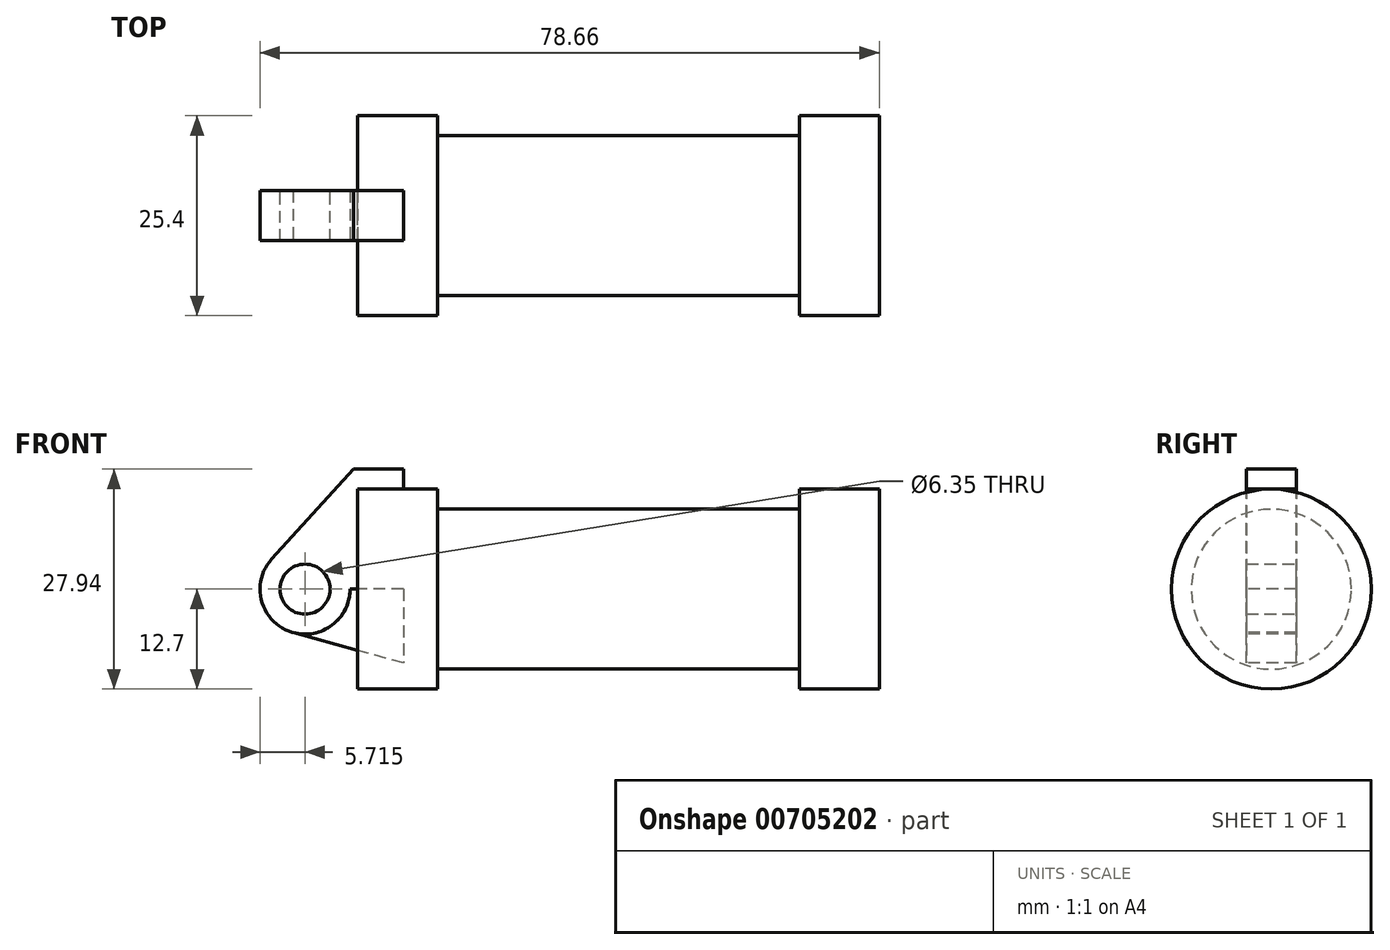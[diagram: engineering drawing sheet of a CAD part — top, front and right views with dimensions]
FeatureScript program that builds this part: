
annotation { "Feature Type Name" : "Feature", "Feature Type Description" : "" }
export const myFeature = defineFeature(function(context is Context, id is Id, definition is map)
    precondition{}
    {
        {
            var Q0;
            Q0=qCreatedBy(makeId("Front.planeOp"),FACE);
            var sketch = newSketch(context, id + "F0", { "sketchPlane" : qUnion([Q0])});
            skLineSegment(sketch, "E0", {"start": v(0, 0) * mm, "end": v(0, 12.7) * mm});
            skLineSegment(sketch, "E1", {"start": v(0, 12.7) * mm, "end": v(10.16, 12.7) * mm});
            skLineSegment(sketch, "E2", {"start": v(10.16, 12.7) * mm, "end": v(10.16, 10.16) * mm});
            skLineSegment(sketch, "E3", {"start": v(10.16, 10.16) * mm, "end": v(56.13, 10.16) * mm});
            skLineSegment(sketch, "E4", {"start": v(56.13, 10.16) * mm, "end": v(56.13, 12.7) * mm});
            skLineSegment(sketch, "E5", {"start": v(56.13, 12.7) * mm, "end": v(66.3, 12.7) * mm});
            skLineSegment(sketch, "E6", {"start": v(66.3, 12.7) * mm, "end": v(66.3, 0) * mm});
            skLineSegment(sketch, "E7", {"start": v(66.3, 0) * mm, "end": v(0, 0) * mm});
            skLineSegment(sketch, "E8", {"start": v(5.84, 15.24) * mm, "end": v(-0.5, 15.24) * mm});
            skLineSegment(sketch, "E9", {"start": v(-0.5, 15.24) * mm, "end": v(-10.88, 3.85) * mm});
            skLineSegment(sketch, "E10", {"start": v(0, 0) * mm, "end": v(-6.65, 0) * mm});
            skCircle(sketch, "E11", {"center": v(-6.65, 0) * mm, "radius": 5.72 * mm});
            skCircle(sketch, "E12", {"center": v(-6.65, 0) * mm, "radius": 3.18 * mm});
            skLineSegment(sketch, "E13", {"start": v(5.84, 15.24) * mm, "end": v(5.84, -9.4) * mm});
            skLineSegment(sketch, "E14", {"start": v(5.84, -9.4) * mm, "end": v(-8.18, -5.5) * mm});
            skSolve(sketch);
        }
        {
            var Q0;
            {var subQ0=sQuery(id+"F0.wireOp",EDGE,"E2");Q0=makeQuery(id+"F0.imprint","IMPRINT",FACE,{"disambiguationData":[TD([[makeQuery(id+"F0.imprint","IMPRINT",EDGE,{"derivedFrom":subQ0}),-1.0]])]});}
            var Q1;
            {var subQ0=sQuery(id+"F0.wireOp",EDGE,"E0");Q1=makeQuery(id+"F0.imprint","IMPRINT",FACE,{"disambiguationData":[TD([[makeQuery(id+"F0.imprint","IMPRINT",EDGE,{"derivedFrom":subQ0}),-1.0]])]});}
            var Q2;
            Q2=sQuery(id+"F0.wireOp",EDGE,"E7");
            revolve(context, id + "F1", {"entities" : qUnion([Q0, Q1]), "axis" : qUnion([Q2]), "revolveType" : RevolveType.FULL});
        }
        {
            var Q0;
            {var subQ0=sQuery(id+"F0.wireOp",EDGE,"E14");Q0=makeQuery(id+"F0.imprint","IMPRINT",FACE,{"disambiguationData":[TD([[makeQuery(id+"F0.imprint","IMPRINT",EDGE,{"derivedFrom":subQ0}),-1.0]])]});}
            var sketch = newSketch(context, id + "F2", { "sketchPlane" : qUnion([Q0])});
            skSolve(sketch);
        }
        {
            var Q0;
            {var subQ5=sQuery(id+"F0.wireOp",EDGE,"E12");Q0=makeQuery(id+"F0.imprint","IMPRINT",FACE,{"disambiguationData":[TD([[makeQuery(id+"F0.imprint","IMPRINT",EDGE,{"derivedFrom":subQ5}),-1.0]])]});}
            var Q1;
            {var subQ1=sQuery(id+"F0.wireOp",EDGE,"E0");Q1=makeQuery(id+"F0.imprint","IMPRINT",FACE,{"disambiguationData":[TD([[makeQuery(id+"F0.imprint","IMPRINT",EDGE,{"derivedFrom":subQ1}),1.0]])]});}
            var Q2;
            {var subQ0=sQuery(id+"F0.wireOp",EDGE,"E14");Q2=makeQuery(id+"F2.imprint","IMPRINT",FACE,{"disambiguationData":[TD([[makeQuery(id+"F2.imprint","IMPRINT",EDGE,{"derivedFrom":makeQuery(id+"F0.imprint","IMPRINT",EDGE,{"derivedFrom":subQ0})}),-1.0]])]});}
            extrude(context, id + "F3", {"entities" : qUnion([Q0, Q1, Q2]), "endBound" : BoundingType.SYMMETRIC, "depth" : 6.35 * mm, "offsetDistance" : 25.4 * mm});
        }
        {
            var Q0;
            Q0=makeQuery(id+"F3.opExtrude","SWEPT_BODY",BODY,{"disambiguationData":[OSD([sQuery(id+"F0.wireOp",EDGE,"E7"),sQuery(id+"F0.wireOp",EDGE,"E10"),sQuery(id+"F0.wireOp",EDGE,"E11"),sQuery(id+"F0.wireOp",EDGE,"E13"),sQuery(id+"F0.wireOp",EDGE,"E14")])]});
            deleteBodies(context, id + "F4", {"entities" : qUnion([Q0])});
        }
        {
            var Q0;
            {var subQ0=sQuery(id+"F0.wireOp",EDGE,"E14");Q0=makeQuery(id+"F0.imprint","IMPRINT",FACE,{"disambiguationData":[TD([[makeQuery(id+"F0.imprint","IMPRINT",EDGE,{"derivedFrom":subQ0}),-1.0]])]});}
            var Q1;
            Q1=makeQuery(id+"F3.opExtrude","CAP_FACE",FACE,{"disambiguationData":[OSD([sQuery(id+"F0.wireOp",EDGE,"E0"),sQuery(id+"F0.wireOp",EDGE,"E1"),sQuery(id+"F0.wireOp",EDGE,"E8"),sQuery(id+"F0.wireOp",EDGE,"E9"),sQuery(id+"F0.wireOp",EDGE,"E10"),sQuery(id+"F0.wireOp",EDGE,"E11"),sQuery(id+"F0.wireOp",EDGE,"E12"),sQuery(id+"F0.wireOp",EDGE,"E13")])],"isStart":true});
            extrude(context, id + "F5", {"entities" : qUnion([Q0]), "endBound" : BoundingType.SYMMETRIC, "oppositeDirection" : true, "depth" : 6.35 * mm, "endBoundEntityFace" : qUnion([Q1]), "offsetDistance" : 25.4 * mm});
        }
    });
